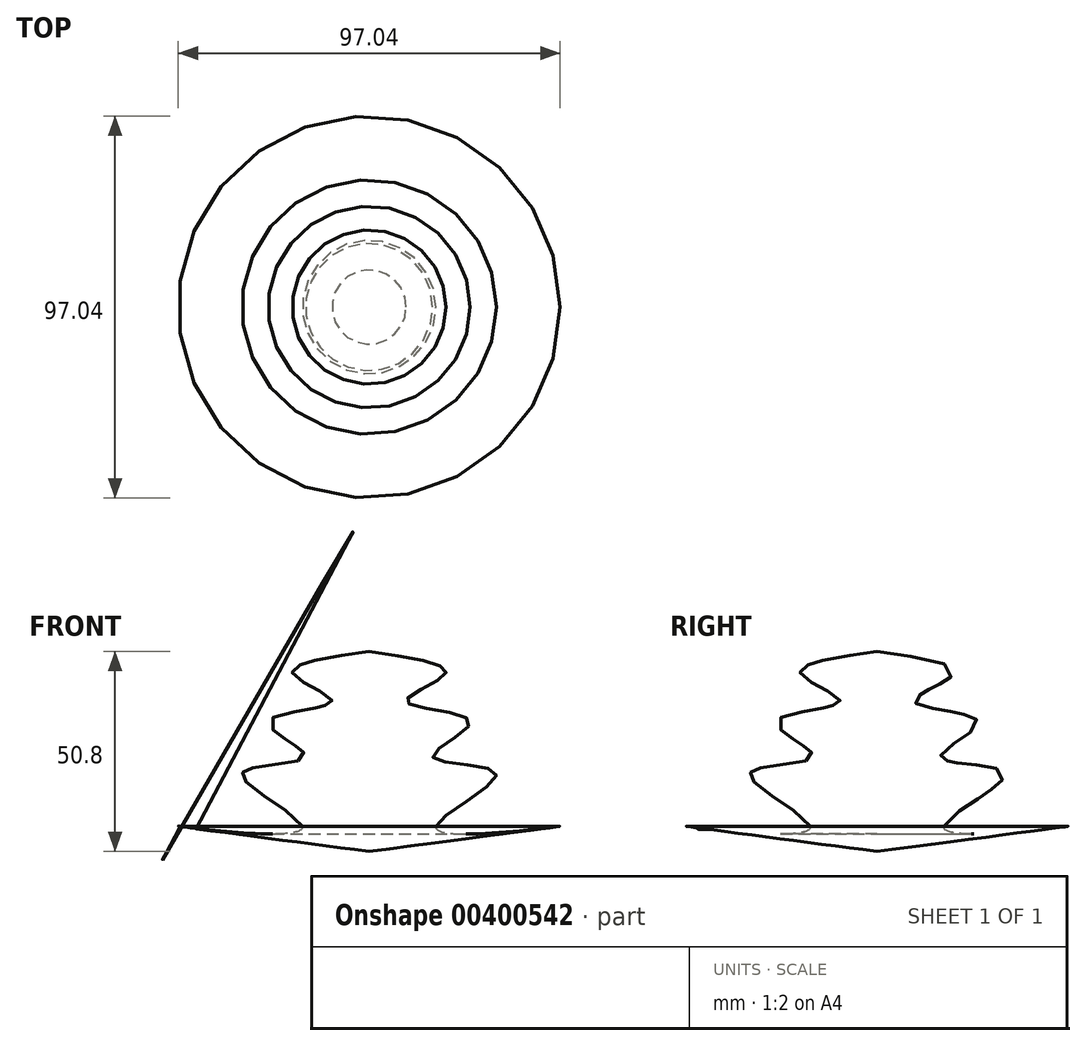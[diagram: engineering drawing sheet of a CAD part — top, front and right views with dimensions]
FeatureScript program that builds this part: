
annotation { "Feature Type Name" : "Feature", "Feature Type Description" : "" }
export const myFeature = defineFeature(function(context is Context, id is Id, definition is map)
    precondition{}
    {
        {
            var Q0;
            Q0=qCreatedBy(makeId("Front.planeOp"),FACE);
            var sketch = newSketch(context, id + "F0", { "sketchPlane" : qUnion([Q0])});
            skLineSegment(sketch, "E0", {"start": v(0, 50.8) * mm, "end": v(0, 0) * mm});
            skFitSpline(sketch, "E1", {"points": [v(0, 50.8) * mm, v(19.31, 44.93) * mm, v(9.46, 38.03) * mm, v(25.62, 32.91) * mm, v(16.16, 24.04) * mm, v(32.32, 19.7) * mm, v(16.95, 6.1) * mm, v(47.7, 6.3) * mm, v(0, 0) * mm], "startDerivative": vector(261.62, -37.19) * mm, "endDerivative": vector(-426.3, -55.74) * mm});
            skSolve(sketch);
        }
        {
            var Q0;
            Q0=sQuery(id+"F0.wireOp",EDGE,"E1");
            var Q1;
            Q1=sQuery(id+"F0.wireOp",EDGE,"E0");
            revolve(context, id + "F1", {"bodyType" : ToolBodyType.SURFACE, "surfaceEntities" : qUnion([Q0]), "axis" : qUnion([Q1]), "revolveType" : RevolveType.FULL});
        }
    });
